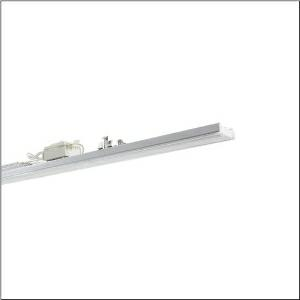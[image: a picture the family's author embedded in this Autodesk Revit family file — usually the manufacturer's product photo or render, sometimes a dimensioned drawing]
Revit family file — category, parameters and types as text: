
# Revit family: licross_r__11_recessed_mo_51tl12mn44xg_8788
name_source: partatom
category: Lighting Fixtures
units: mm (PartAtom-declared; Revit-internal decimal feet)

## family parameters
Cut with Voids When Loaded = No
Host = Face
Light Source = No
Part Type = Normal
Room Calculation Point = No
Round Connector Dimension = Use Diameter
Shared = No

## types (1)
- Licross® 11 Recessed MO (1 x LED, 4300 lm, 21.9 W, 4000K)
    Apparent Load = 22 VA
    CIE Flux Codes = 67 92 99 100 100
    Color Rendering = 80
    Color Temperature = 4000K
    Default Elevation = 1800 mm
    Description = Licross® 11 Recessed MO, luminaire insert, of sheet steel, coil coated, white, length: 1.500mm, width: 66mm, height: 67mm, LED rated luminous flux: 4.300lm, light colour: 840, control gear: ON/OFF, with plug, 3-pole, with phase selection, mains connection: 220..240V, AC, 50/60Hz, rated input power: 22W, halogen-free wiring, primary optical cover: cover, of PMMA, light emission: direct distribution, primary light characteristic: symmetric, protection rating (complete): IP40, insulation class (complete): insulation class I (protective earthing), certification: CE, ENEC, VDE, UKCA, protection symbol: D if used in an environment without relevant dust loads with corresponding accessories, impact resistance: IK06, permissible ambient temperature for indoor applications: -35..+55°C, corresponds to IFS (International Featured Standards) requirements for safety and quality in the food industry, reducing of maximum allowable ambient temperature of 5°C with ceiling mounting, packaging unit: 1 piece
    Height = 58 mm
    Lamp = 1 x LED
    Lamp Light Flux = 4300 lm
    Lamp Power = 21.9 W
    Lamp count = 1
    Length = 1500 mm
    Luminous efficacy = 196 lm/W
    Manufacturer = Siteco
    ModVariant = No
    Model = 51TL12MN44XG
    Mounting Place = Ceiling
    Mounting Type = Pendant
    Number of Poles = 1
    OnlyDefault = Yes
    Power Factor = 1
    Product Name = Licross® 11 Recessed MO
    Product group = luminaire insert
    ProductGroupID = 902
    Protection Class = Protection class I
    Protection Degree = IP 40
    RLX_Detail_Level = 1
    RLX_Emergency_Light_Flux = 0 lm
    RLX_Emergency_Type = 0
    RLX_Emergency_Type_DB = No
    RlxData = <blob elided: 20697 chars, md5=761a0027>
    Socket = socket
    Standby Power = 0 W
    System Light Flux = 4300 lm
    System Power = 22 W
    Type Comments = Product without accessories
    Type Image = l_1296930.jpg
    URL = http://relux.com
    VarID = ---
    Voltage = 0 V
    Weight = 0.00 kg
    Width = 66 mm

## geometry (parser evidence)
native form markers: Blend x4, Sweep x11
no freeform markers — native parametric forms only
